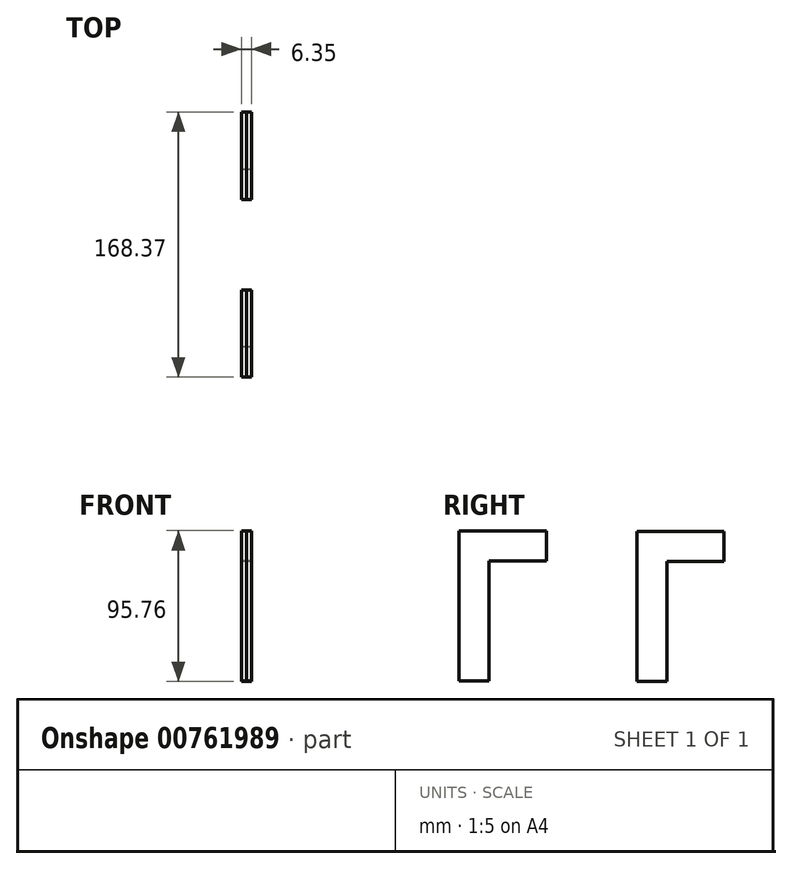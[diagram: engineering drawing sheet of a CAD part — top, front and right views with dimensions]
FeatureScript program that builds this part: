
annotation { "Feature Type Name" : "Feature", "Feature Type Description" : "" }
export const myFeature = defineFeature(function(context is Context, id is Id, definition is map)
    precondition{}
    {
        {
            var Q0;
            Q0=qCreatedBy(makeId("Right.planeOp"),FACE);
            var sketch = newSketch(context, id + "F0", { "sketchPlane" : qUnion([Q0])});
            skLineSegment(sketch, "E0", {"start": v(-42.86, 86.9) * mm, "end": v(-66.58, 86.9) * mm});
            skLineSegment(sketch, "E1", {"start": v(-66.58, 86.9) * mm, "end": v(-66.58, -8.34) * mm});
            skLineSegment(sketch, "E2", {"start": v(-66.58, -8.34) * mm, "end": v(-47.53, -8.34) * mm});
            skLineSegment(sketch, "E3", {"start": v(-47.53, -8.34) * mm, "end": v(-47.53, 67.86) * mm});
            skLineSegment(sketch, "E4", {"start": v(-47.53, 67.86) * mm, "end": v(-11.1, 67.86) * mm});
            skLineSegment(sketch, "E5", {"start": v(-11.1, 67.86) * mm, "end": v(-11.1, 86.9) * mm});
            skLineSegment(sketch, "E6", {"start": v(-11.1, 86.9) * mm, "end": v(-42.86, 86.9) * mm});
            skLineSegment(sketch, "E7", {"start": v(70.04, 86.4) * mm, "end": v(46.32, 86.4) * mm});
            skLineSegment(sketch, "E8", {"start": v(46.32, 86.4) * mm, "end": v(46.32, -8.85) * mm});
            skLineSegment(sketch, "E9", {"start": v(46.32, -8.85) * mm, "end": v(65.37, -8.85) * mm});
            skLineSegment(sketch, "E10", {"start": v(65.37, -8.85) * mm, "end": v(65.37, 67.35) * mm});
            skLineSegment(sketch, "E11", {"start": v(65.37, 67.35) * mm, "end": v(101.8, 67.35) * mm});
            skLineSegment(sketch, "E12", {"start": v(101.8, 67.35) * mm, "end": v(101.8, 86.4) * mm});
            skLineSegment(sketch, "E13", {"start": v(101.8, 86.4) * mm, "end": v(70.04, 86.4) * mm});
            skSolve(sketch);
        }
        {
            var Q0;
            Q0=makeQuery(id+"F0.imprint","IMPRINT",FACE,{"disambiguationData":[TD([[makeQuery(id+"F0.imprint","IMPRINT",EDGE,{"derivedFrom":sQuery(id+"F0.wireOp",EDGE,"E0")}),1.0]])]});
            var Q1;
            Q1=makeQuery(id+"F0.imprint","IMPRINT",FACE,{"disambiguationData":[TD([[makeQuery(id+"F0.imprint","IMPRINT",EDGE,{"derivedFrom":sQuery(id+"F0.wireOp",EDGE,"E7")}),1.0]])]});
            extrude(context, id + "F1", {"entities" : qUnion([Q0, Q1]), "depth" : 3.17 * mm, "offsetDistance" : 25.4 * mm});
        }
        {
            var Q0;
            Q0=makeQuery(id+"F1.opExtrude","CAP_FACE",FACE,{"disambiguationData":[OSD([sQuery(id+"F0.wireOp",EDGE,"E0"),sQuery(id+"F0.wireOp",EDGE,"E1"),sQuery(id+"F0.wireOp",EDGE,"E2"),sQuery(id+"F0.wireOp",EDGE,"E3"),sQuery(id+"F0.wireOp",EDGE,"E4"),sQuery(id+"F0.wireOp",EDGE,"E5"),sQuery(id+"F0.wireOp",EDGE,"E6")])],"isStart":false});
            var Q1;
            Q1=makeQuery(id+"F1.opExtrude","CAP_FACE",FACE,{"disambiguationData":[OSD([sQuery(id+"F0.wireOp",EDGE,"E7"),sQuery(id+"F0.wireOp",EDGE,"E8"),sQuery(id+"F0.wireOp",EDGE,"E9"),sQuery(id+"F0.wireOp",EDGE,"E10"),sQuery(id+"F0.wireOp",EDGE,"E11"),sQuery(id+"F0.wireOp",EDGE,"E12"),sQuery(id+"F0.wireOp",EDGE,"E13")])],"isStart":false});
            extrude(context, id + "F2", {"entities" : qUnion([Q0, Q1]), "depth" : 3.17 * mm, "offsetDistance" : 25.4 * mm});
        }
    });
